# Revit family: AS_0630_50_S22_4D
name_source: partatom
category: Mechanical Equipment
revit_build: Autodesk Revit 2018 (Build: 20170223_1515(x64)
units: mm (PartAtom-declared; Revit-internal decimal feet)

## family parameters
Always vertical = Yes
Cut with Voids When Loaded = No
Part Type = Normal
Room Calculation Point = No
Round Connector Dimension = Use Radius
Shared = No
Work Plane-Based = No

## types (1)
- AS0630 S22/4D
    Bottom Plate = Cast Iron EN-GJL-250
    Cable Length (m) = As per Specification
    Cable Size = Standard = 4G1.5, Ex = 7G1.5
    Capacity (m3/hr) = 80 m³
    Description = Robust, reliable submersible pumps from 1 to 3 kW for
pumping clear water, wastewater and sewage from buildings
and sites in domestic and commercial areas.

with EN 12050-1. The Piranhamat 1002 is used for reliable and
economical discharge of wastewater under pressure using
small diameter discharge lines. Suitable for new installations
or for renovation of old buildings.
    Discharge Connection = DN65
    Discharge DN 65 = 33 mm
    Fasteners = Stainless steel 1.4401 (AISI 316)
    Head (m) = 35 mm  [stored 0.114829 ft]
    Impeller = Cast Iron EN-GJL-250
    Manufacturer = Sulzer
    Model = Submersible Wastewater Pump Type ABS AS 0630
    Motor Housing = Cast Iron EN-GJL-250
    Motor Power (kW) = P1=2.88 P2=2.20
    Product Specification Link = https://www.sulzer.com
    Rated Current (A) = 5.15
    Rated Voltage (V) = 400 3~
    Rotor Shaft = Stainless steel 1.4021 (AISI 420)
    Solids Size = 60
    Speed (r/min) = 1450
    Volute = Cast Iron EN-GJL-250

note: [stored X ft] marks values corroborated as IEEE doubles in the binary element streams (Revit-internal decimal feet)

## geometry (parser evidence)
native form markers: Sweep x3
no freeform markers — native parametric forms only
